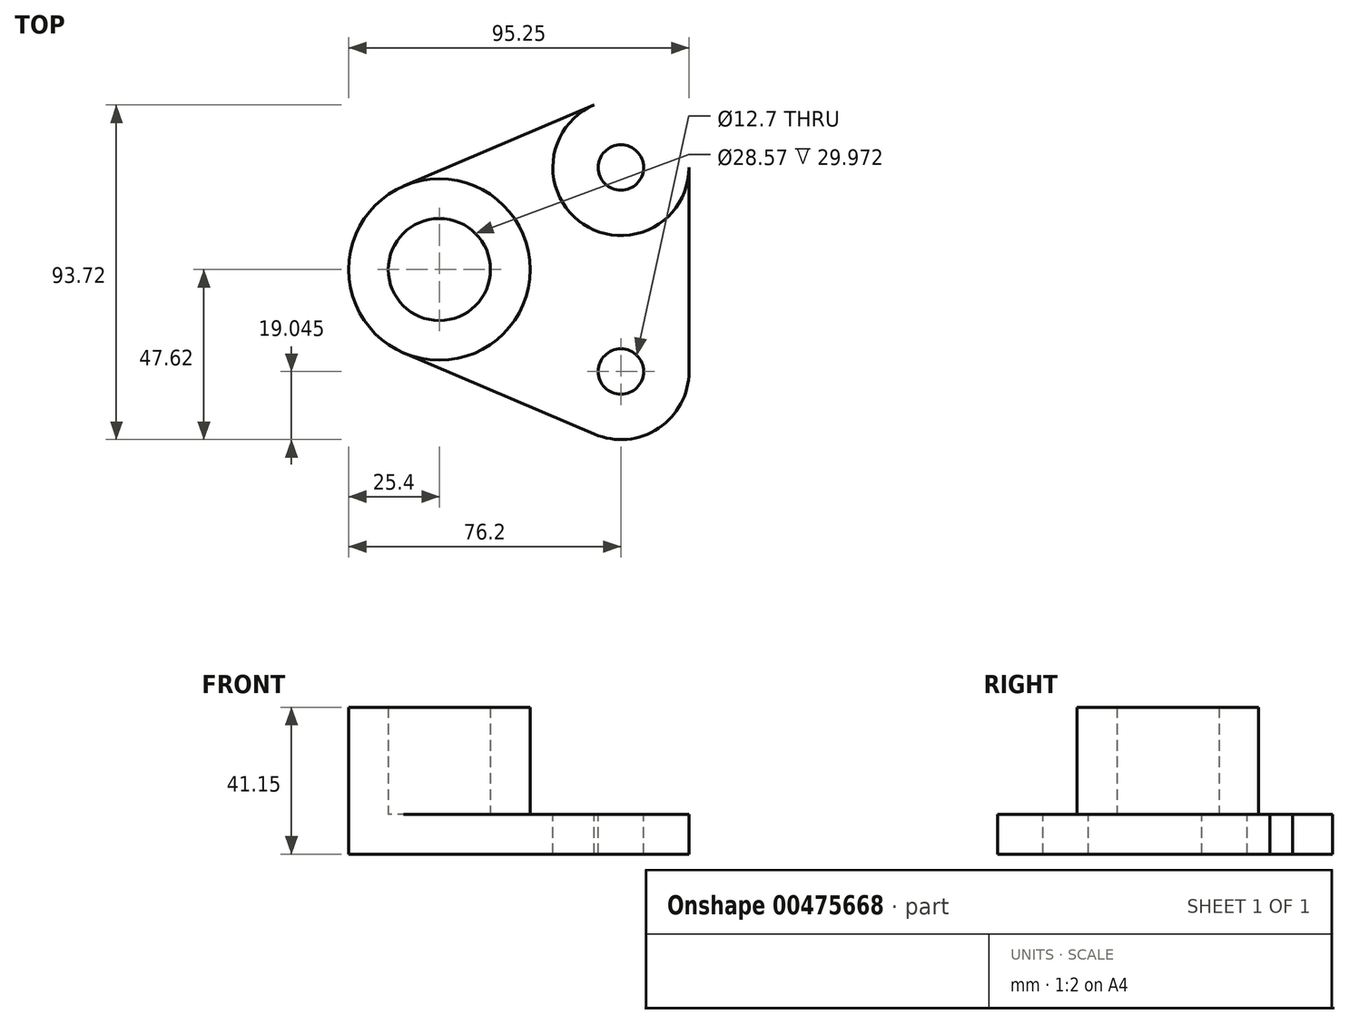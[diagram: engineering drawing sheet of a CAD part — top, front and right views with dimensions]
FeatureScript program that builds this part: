
annotation { "Feature Type Name" : "Feature", "Feature Type Description" : "" }
export const myFeature = defineFeature(function(context is Context, id is Id, definition is map)
    precondition{}
    {
        {
            var Q0;
            Q0=qCreatedBy(makeId("Top.planeOp"),FACE);
            var sketch = newSketch(context, id + "F0", { "sketchPlane" : qUnion([Q0])});
            skCircle(sketch, "E0", {"center": v(-50.8, 0) * mm, "radius": 25.4 * mm});
            skCircle(sketch, "E1", {"center": v(0, -28.58) * mm, "radius": 6.35 * mm});
            skCircle(sketch, "E2.MirrorC", {"center": v(0, 28.58) * mm, "radius": 6.35 * mm});
            skCircle(sketch, "E3", {"center": v(0, 28.58) * mm, "radius": 19.05 * mm});
            skCircle(sketch, "E4", {"center": v(0, -28.58) * mm, "radius": 19.05 * mm});
            skLineSegment(sketch, "E5", {"start": v(-60.77, 23.36) * mm, "end": v(-7.47, 46.1) * mm});
            skLineSegment(sketch, "E6", {"start": v(19.05, 28.58) * mm, "end": v(19.05, -28.58) * mm});
            skLineSegment(sketch, "E7", {"start": v(-60.77, -23.36) * mm, "end": v(-7.47, -46.1) * mm});
            skCircle(sketch, "E8", {"center": v(-50.8, 0) * mm, "radius": 14.29 * mm});
            skLineSegment(sketch, "E9", {"start": v(15.75, 3.22) * mm, "end": v(15.75, -3.13) * mm});
            skSolve(sketch);
        }
        {
            var Q0;
            {var subQ0=sQuery(id+"F0.wireOp",EDGE,"E5");Q0=makeQuery(id+"F0.imprint","IMPRINT",FACE,{"disambiguationData":[TD([[makeQuery(id+"F0.imprint","IMPRINT",EDGE,{"derivedFrom":subQ0}),-1.0]])]});}
            var Q1;
            Q1=makeQuery(id+"F0.imprint","IMPRINT",FACE,{"disambiguationData":[TD([[makeQuery(id+"F0.imprint","IMPRINT",EDGE,{"derivedFrom":sQuery(id+"F0.wireOp",EDGE,"E2.MirrorC")}),1.0]])]});
            var Q2;
            Q2=makeQuery(id+"F0.imprint","IMPRINT",FACE,{"disambiguationData":[TD([[makeQuery(id+"F0.imprint","IMPRINT",EDGE,{"derivedFrom":sQuery(id+"F0.wireOp",EDGE,"E1")}),-1.0]])]});
            var Q3;
            Q3=makeQuery(id+"F0.imprint","IMPRINT",FACE,{"disambiguationData":[TD([[makeQuery(id+"F0.imprint","IMPRINT",EDGE,{"derivedFrom":sQuery(id+"F0.wireOp",EDGE,"E8")}),-1.0]])]});
            var Q4;
            Q4=makeQuery(id+"F0.imprint","IMPRINT",FACE,{"disambiguationData":[TD([[makeQuery(id+"F0.imprint","IMPRINT",EDGE,{"derivedFrom":sQuery(id+"F0.wireOp",EDGE,"E8")}),1.0]])]});
            extrude(context, id + "F1", {"entities" : qUnion([Q0, Q1, Q2, Q3, Q4]), "oppositeDirection" : true, "depth" : 11.18 * mm});
        }
        {
            var Q0;
            Q0=makeQuery(id+"F0.imprint","IMPRINT",FACE,{"disambiguationData":[TD([[makeQuery(id+"F0.imprint","IMPRINT",EDGE,{"derivedFrom":sQuery(id+"F0.wireOp",EDGE,"E8")}),-1.0]])]});
            extrude(context, id + "F2", {"entities" : qUnion([Q0]), "operationType" : NewBodyOperationType.ADD, "depth" : 29.97 * mm});
        }
    });
